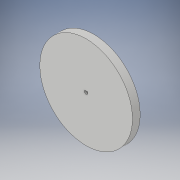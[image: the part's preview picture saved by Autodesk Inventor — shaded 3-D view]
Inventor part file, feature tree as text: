
AUTODESK INVENTOR PART (.ipt)
format: ipt  version: 2018.1 (Build 221171000, 171)  size: 108,544 bytes
history: native  units: in
note: dims shown in document units (in); Inventor stores cm internally (conversion verified against a paired STEP export)
features: sketch x2, other x2, sheet_metal_op x1
ambient origin geometry x8: Origin, YZ Plane, XZ Plane, XY Plane, X Axis, Y Axis, Z Axis, Center Point
bodies: Solid1 (feature_tree)
feature tree (5):
  sheet_metal_op  "Face1"
  sketch  "Sketch1"  dims[d0=3.0in]
  other  "Plate1"
  sketch  "Sketch2"  dims[d1=0.25in d2=0.116in d4=0.096in d5=0.25in d6=0.0in]
  other  "Cut1"
